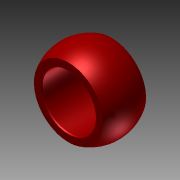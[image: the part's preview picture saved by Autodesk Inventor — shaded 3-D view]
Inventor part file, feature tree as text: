
AUTODESK INVENTOR PART (.ipt)
format: ipt  version: 2011 (Build 150239000, 239)  size: 106,496 bytes
history: native  units: mm (DEFAULTED — no unit token found)
features: sketch x2, revolve x1, extrude x1, hole x1, chamfer x1
ambient origin geometry x8: Origin, YZ Plane, XZ Plane, XY Plane, X Axis, Y Axis, Z Axis, Center Point
bodies: Solid1 (feature_tree)
feature tree (6):
  revolve  "Revolution1"  Angle=90.0deg
  extrude  "Extrusion3"  Depth=25.4mm TaperAngle=0.0deg
  hole  "Hole1"  [1 undecoded]
  chamfer  "Chamfer1"  Distance=0.3048mm Angle=30.0deg
  sketch  "Sketch1"  dims[d0=24.003mm d1=90.0deg]
  sketch  "Sketch4"  dims[d8=12.7mm d9=25.4mm d10=0.0mm d11=25.4mm d12=25.4mm d13=15.875mm d14=12.7mm d15=9.525mm d16=6.35mm d17=14.3117mm d18=19.05mm d19=20.594885mm d20=0.3048mm d21=3.175mm d22=30.0deg]
note: 1 required parameter value undecoded (feature->parameter linkage not recoverable at this tier; creation-order binding heuristic only, values carry confidence <= 0.55)
